# Revit family: 879-106X99-001-DN50-250
name_source: partatom
category: Pipe Accessories
units: mm (PartAtom-declared; Revit-internal decimal feet)

## family parameters
Always vertical = Yes
Cut with Voids When Loaded = No
Part Type = Valve - Breaks Into
Round Connector Dimension = Use Diameter
Shared = No
Work Plane-Based = No

## types (36) — shared parameters
879-0050-10-14400609999 = DN50_PN10/16
879-0050-10-14400619999 = DN50_PN10/16
879-0050-10-14400629999 = DN50_PN10/16
879-0050-10-144006299A0 = DN50_PN10/16
879-0065-10-14400609999 = DN65_PN10/16
879-0065-10-14400619999 = DN65_PN10/16
879-0065-10-14400629999 = DN65_PN10/16
879-0065-10-144006299A0 = DN65_PN10/16
879-0080-10-14400609999 = DN80_PN10/16
879-0080-10-14400619999 = DN80_PN10/16
879-0080-10-14400629999 = DN80_PN10/16
879-0080-10-144006299A0 = DN80_PN10/16
879-0100-10-14400609999 = DN100_PN10/16
879-0100-10-14400619999 = DN100_PN10/16
879-0100-10-14400629999 = DN100_PN10/16
879-0100-10-144006299A0 = DN100_PN10/16
879-0150-10-14400609999 = DN150_PN10/16
879-0150-10-14400619999 = DN150_PN10/16
879-0150-10-14400629999 = DN150_PN10/16
879-0150-10-144006299A0 = DN150_PN10/16
879-0200-10-04400609999 = DN200_PN10
879-0200-10-04400619999 = DN200_PN10
879-0200-10-04400629999 = DN200_PN10
879-0200-10-044006299A0 = DN200_PN10
879-0200-10-14400609999 = DN200_PN16
879-0200-10-14400619999 = DN200_PN16
879-0200-10-14400629999 = DN200_PN16
879-0200-10-144006299A0 = DN200_PN16
879-0250-10-04400609999 = DN250_PN10
879-0250-10-04400619999 = DN250_PN10
879-0250-10-04400629999 = DN250_PN10
879-0250-10-044006299A0 = DN250_PN10
879-0250-10-14400609999 = DN250_PN16
879-0250-10-14400619999 = DN250_PN16
879-0250-10-14400629999 = DN250_PN16
879-0250-10-144006299A0 = DN250_PN16
Body_wall_thickness = 10 mm  [stored 0.0328084 ft]
Description_ = AVK ON/OFF FLOAT LEVEL CONTROL VALVE
Search_Table = 879-106X99-001-DN50-250
URL product pages = https://www.avkvalves.com

## per-type parameters (varying)
- 879-0050-10-14400609999_DN50_PN10/16: Body_Collar_Dia=24 mm  [stored 0.0787402 ft]; Body_Collar_Dia_2=21 mm  [stored 0.0688976 ft]; Body_Flange_Dia=74 mm; Body_Flange_Dia_2=82 mm; Body_Height_1=58 mm; Body_Height_2=29 mm; Body_Height_3=45 mm; Body_Height_4=44 mm; Body_Top_Dia=10 mm  [stored 0.0328084 ft]; Body_Top_Dia_2=9 mm  [stored 0.0295276 ft]; Body_With_Dia=29 mm; Body_With_Dia_1=58 mm; Body_With_Dia_2=62 mm; Bolt_support=177 mm; Bolt_support_2=88 mm; Bolt_support_Dia=12 mm  [stored 0.0393701 ft]; Bolt_support_lenght=45 mm; Bolt_support_lenght_2=55 mm; Bottom_profile=13 mm; D1=50 mm; D3=83 mm; DN=50 mm; Fillet_Length=6 mm  [stored 0.019685 ft]; Fillet_Length_Ref=18 mm  [stored 0.0590551 ft]; Flange_thickness=19 mm  [stored 0.062336 ft]; H=290 mm; H3_Ref=284 mm; ID=25 mm  [stored 0.082021 ft]; L=230 mm; PG_Dia=25 mm  [stored 0.082021 ft]; PG_Ref=38 mm; PG_depth=8 mm  [stored 0.0262467 ft]; PG_height=180 mm; PG_height_1=167 mm; PG_ref=35 mm  [stored 0.114829 ft]; PR_1=14 mm  [stored 0.0459318 ft]; P_lenght=33 mm  [stored 0.108268 ft]; Pilot_Dia_1=15 mm  [stored 0.0492126 ft]; Pilot_Dia_2=30 mm  [stored 0.0984252 ft]; Pilot_Dia_3=10 mm  [stored 0.0328084 ft]; Pilot_Dia_4=5 mm  [stored 0.0164042 ft]; Pilot_Dia_5=3 mm  [stored 0.00984252 ft]; Pilot_top_1=174 mm; Pilot_top_ref=18 mm  [stored 0.0590551 ft]; Profile1_Height=100 mm; Profile1_Length=22 mm  [stored 0.0721785 ft]; Profile1_Length_2=15 mm  [stored 0.0492126 ft]; Profile_Dia=6 mm  [stored 0.019685 ft]; Profile_Dia_2=6 mm  [stored 0.019685 ft]; Profile_Dia_3=12 mm  [stored 0.0393701 ft]; Profile_height ref=41 mm; T_Height=61 mm; T_Height_2=52 mm; T_Height_Ref_1=9 mm  [stored 0.0295276 ft]; T_Height_Ref_2=10 mm  [stored 0.0328084 ft]; Top_Profile=106 mm; Top_Profile_Ref=111 mm; W=252 mm; W_Ref=246 mm
- 879-0050-10-14400619999_DN50_PN10/16: Body_Collar_Dia=24 mm  [stored 0.0787402 ft]; Body_Collar_Dia_2=21 mm  [stored 0.0688976 ft]; Body_Flange_Dia=74 mm; Body_Flange_Dia_2=82 mm; Body_Height_1=58 mm; Body_Height_2=29 mm; Body_Height_3=50 mm; Body_Height_4=44 mm; Body_Top_Dia=10 mm  [stored 0.0328084 ft]; Body_Top_Dia_2=9 mm  [stored 0.0295276 ft]; Body_With_Dia=29 mm; Body_With_Dia_1=58 mm; Body_With_Dia_2=62 mm; Bolt_support=177 mm; Bolt_support_2=88 mm; Bolt_support_Dia=12 mm  [stored 0.0393701 ft]; Bolt_support_lenght=45 mm; Bolt_support_lenght_2=55 mm; Bottom_profile=13 mm; D1=50 mm; D3=83 mm; DN=50 mm; Fillet_Length=6 mm  [stored 0.019685 ft]; Fillet_Length_Ref=18 mm  [stored 0.0590551 ft]; Flange_thickness=19 mm  [stored 0.062336 ft]; H=290 mm; H3_Ref=284 mm; ID=25 mm  [stored 0.082021 ft]; L=230 mm; PG_Dia=25 mm  [stored 0.082021 ft]; PG_Ref=38 mm; PG_depth=8 mm  [stored 0.0262467 ft]; PG_height=187 mm; PG_height_1=175 mm; PG_ref=35 mm  [stored 0.114829 ft]; PR_1=11 mm; P_lenght=33 mm  [stored 0.108268 ft]; Pilot_Dia_1=15 mm  [stored 0.0492126 ft]; Pilot_Dia_2=30 mm  [stored 0.0984252 ft]; Pilot_Dia_3=10 mm  [stored 0.0328084 ft]; Pilot_Dia_4=5 mm  [stored 0.0164042 ft]; Pilot_Dia_5=3 mm  [stored 0.00984252 ft]; Pilot_top_1=176 mm; Pilot_top_ref=15 mm  [stored 0.0492126 ft]; Profile1_Height=110 mm; Profile1_Length=22 mm  [stored 0.0721785 ft]; Profile1_Length_2=15 mm  [stored 0.0492126 ft]; Profile_Dia=6 mm  [stored 0.019685 ft]; Profile_Dia_2=6 mm  [stored 0.019685 ft]; Profile_Dia_3=12 mm  [stored 0.0393701 ft]; Profile_height ref=41 mm; T_Height=51 mm; T_Height_2=43 mm; T_Height_Ref_1=7 mm  [stored 0.0229659 ft]; T_Height_Ref_2=8 mm  [stored 0.0262467 ft]; Top_Profile=106 mm; Top_Profile_Ref=111 mm; W=252 mm; W_Ref=246 mm
- 879-0050-10-14400629999_DN50_PN10/16: Body_Collar_Dia=24 mm  [stored 0.0787402 ft]; Body_Collar_Dia_2=21 mm  [stored 0.0688976 ft]; Body_Flange_Dia=74 mm; Body_Flange_Dia_2=82 mm; Body_Height_1=58 mm; Body_Height_2=29 mm; Body_Height_3=45 mm; Body_Height_4=44 mm; Body_Top_Dia=10 mm  [stored 0.0328084 ft]; Body_Top_Dia_2=9 mm  [stored 0.0295276 ft]; Body_With_Dia=29 mm; Body_With_Dia_1=58 mm; Body_With_Dia_2=62 mm; Bolt_support=177 mm; Bolt_support_2=88 mm; Bolt_support_Dia=12 mm  [stored 0.0393701 ft]; Bolt_support_lenght=45 mm; Bolt_support_lenght_2=55 mm; Bottom_profile=13 mm; D1=50 mm; D3=83 mm; DN=50 mm; Fillet_Length=6 mm  [stored 0.019685 ft]; Fillet_Length_Ref=18 mm  [stored 0.0590551 ft]; Flange_thickness=19 mm  [stored 0.062336 ft]; H=290 mm; H3_Ref=284 mm; ID=25 mm  [stored 0.082021 ft]; L=230 mm; PG_Dia=25 mm  [stored 0.082021 ft]; PG_Ref=38 mm; PG_depth=8 mm  [stored 0.0262467 ft]; PG_height=180 mm; PG_height_1=167 mm; PG_ref=35 mm  [stored 0.114829 ft]; PR_1=14 mm  [stored 0.0459318 ft]; P_lenght=33 mm  [stored 0.108268 ft]; Pilot_Dia_1=15 mm  [stored 0.0492126 ft]; Pilot_Dia_2=30 mm  [stored 0.0984252 ft]; Pilot_Dia_3=10 mm  [stored 0.0328084 ft]; Pilot_Dia_4=5 mm  [stored 0.0164042 ft]; Pilot_Dia_5=3 mm  [stored 0.00984252 ft]; Pilot_top_1=174 mm; Pilot_top_ref=18 mm  [stored 0.0590551 ft]; Profile1_Height=100 mm; Profile1_Length=22 mm  [stored 0.0721785 ft]; Profile1_Length_2=15 mm  [stored 0.0492126 ft]; Profile_Dia=6 mm  [stored 0.019685 ft]; Profile_Dia_2=6 mm  [stored 0.019685 ft]; Profile_Dia_3=12 mm  [stored 0.0393701 ft]; Profile_height ref=41 mm; T_Height=61 mm; T_Height_2=52 mm; T_Height_Ref_1=9 mm  [stored 0.0295276 ft]; T_Height_Ref_2=10 mm  [stored 0.0328084 ft]; Top_Profile=106 mm; Top_Profile_Ref=111 mm; W=252 mm; W_Ref=246 mm
- 879-0050-10-144006299A0_DN50_PN10/16: Body_Collar_Dia=24 mm  [stored 0.0787402 ft]; Body_Collar_Dia_2=21 mm  [stored 0.0688976 ft]; Body_Flange_Dia=74 mm; Body_Flange_Dia_2=82 mm; Body_Height_1=58 mm; Body_Height_2=29 mm; Body_Height_3=50 mm; Body_Height_4=44 mm; Body_Top_Dia=10 mm  [stored 0.0328084 ft]; Body_Top_Dia_2=9 mm  [stored 0.0295276 ft]; Body_With_Dia=29 mm; Body_With_Dia_1=58 mm; Body_With_Dia_2=62 mm; Bolt_support=177 mm; Bolt_support_2=88 mm; Bolt_support_Dia=12 mm  [stored 0.0393701 ft]; Bolt_support_lenght=45 mm; Bolt_support_lenght_2=55 mm; Bottom_profile=13 mm; D1=50 mm; D3=83 mm; DN=50 mm; Fillet_Length=6 mm  [stored 0.019685 ft]; Fillet_Length_Ref=18 mm  [stored 0.0590551 ft]; Flange_thickness=19 mm  [stored 0.062336 ft]; H=407 mm; H3_Ref=401 mm; ID=25 mm  [stored 0.082021 ft]; L=230 mm; PG_Dia=25 mm  [stored 0.082021 ft]; PG_Ref=38 mm; PG_depth=8 mm  [stored 0.0262467 ft]; PG_height=214 mm; PG_height_1=201 mm; PG_ref=35 mm  [stored 0.114829 ft]; PR_1=38 mm; P_lenght=33 mm  [stored 0.108268 ft]; Pilot_Dia_1=15 mm  [stored 0.0492126 ft]; Pilot_Dia_2=30 mm  [stored 0.0984252 ft]; Pilot_Dia_3=10 mm  [stored 0.0328084 ft]; Pilot_Dia_4=5 mm  [stored 0.0164042 ft]; Pilot_Dia_5=3 mm  [stored 0.00984252 ft]; Pilot_top_1=235 mm; Pilot_top_ref=74 mm; Profile1_Height=110 mm; Profile1_Length=22 mm  [stored 0.0721785 ft]; Profile1_Length_2=15 mm  [stored 0.0492126 ft]; Profile_Dia=6 mm  [stored 0.019685 ft]; Profile_Dia_2=6 mm  [stored 0.019685 ft]; Profile_Dia_3=12 mm  [stored 0.0393701 ft]; Profile_height ref=41 mm; T_Height=168 mm; T_Height_2=144 mm; T_Height_Ref_1=24 mm  [stored 0.0787402 ft]; T_Height_Ref_2=28 mm; Top_Profile=106 mm; Top_Profile_Ref=111 mm; W=252 mm; W_Ref=246 mm
- 879-0065-10-14400609999_DN65_PN10/16: Body_Collar_Dia=30 mm  [stored 0.0984252 ft]; Body_Collar_Dia_2=26 mm; Body_Flange_Dia=94 mm; Body_Flange_Dia_2=104 mm; Body_Height_1=73 mm; Body_Height_2=36 mm; Body_Height_3=58 mm; Body_Height_4=51 mm; Body_Top_Dia=13 mm; Body_Top_Dia_2=11 mm; Body_With_Dia=36 mm; Body_With_Dia_1=73 mm; Body_With_Dia_2=78 mm; Bolt_support=223 mm; Bolt_support_2=112 mm; Bolt_support_Dia=12 mm  [stored 0.0393701 ft]; Bolt_support_lenght=53 mm; Bolt_support_lenght_2=63 mm; Bottom_profile=16 mm  [stored 0.0524934 ft]; D1=59 mm; D3=93 mm; DN=65 mm; Fillet_Length=6 mm  [stored 0.019685 ft]; Fillet_Length_Ref=18 mm  [stored 0.0590551 ft]; Flange_thickness=19 mm  [stored 0.062336 ft]; H=305 mm; H3_Ref=299 mm; ID=33 mm  [stored 0.108268 ft]; L=290 mm; PG_Dia=33 mm  [stored 0.108268 ft]; PG_Ref=48 mm; PG_depth=8 mm  [stored 0.0262467 ft]; PG_height=201 mm; PG_height_1=185 mm; PG_ref=43 mm; PR_1=11 mm; P_lenght=39 mm  [stored 0.127953 ft]; Pilot_Dia_1=18 mm  [stored 0.0590551 ft]; Pilot_Dia_2=35 mm  [stored 0.114829 ft]; Pilot_Dia_3=12 mm  [stored 0.0393701 ft]; Pilot_Dia_4=6 mm  [stored 0.019685 ft]; Pilot_Dia_5=4 mm  [stored 0.0131234 ft]; Pilot_top_1=194 mm; Pilot_top_ref=2 mm  [stored 0.00656168 ft]; Profile1_Height=117 mm; Profile1_Length=25 mm  [stored 0.082021 ft]; Profile1_Length_2=17 mm; Profile_Dia=6 mm  [stored 0.019685 ft]; Profile_Dia_2=6 mm  [stored 0.019685 ft]; Profile_Dia_3=12 mm  [stored 0.0393701 ft]; Profile_height ref=41 mm; T_Height=49 mm; T_Height_2=42 mm; T_Height_Ref_1=7 mm  [stored 0.0229659 ft]; T_Height_Ref_2=8 mm  [stored 0.0262467 ft]; Top_Profile=134 mm; Top_Profile_Ref=139 mm; W=275 mm; W_Ref=269 mm
- 879-0065-10-14400619999_DN65_PN10/16: Body_Collar_Dia=30 mm  [stored 0.0984252 ft]; Body_Collar_Dia_2=26 mm; Body_Flange_Dia=94 mm; Body_Flange_Dia_2=104 mm; Body_Height_1=73 mm; Body_Height_2=36 mm; Body_Height_3=58 mm; Body_Height_4=51 mm; Body_Top_Dia=13 mm; Body_Top_Dia_2=11 mm; Body_With_Dia=36 mm; Body_With_Dia_1=73 mm; Body_With_Dia_2=78 mm; Bolt_support=223 mm; Bolt_support_2=112 mm; Bolt_support_Dia=12 mm  [stored 0.0393701 ft]; Bolt_support_lenght=53 mm; Bolt_support_lenght_2=63 mm; Bottom_profile=16 mm  [stored 0.0524934 ft]; D1=59 mm; D3=93 mm; DN=65 mm; Fillet_Length=6 mm  [stored 0.019685 ft]; Fillet_Length_Ref=18 mm  [stored 0.0590551 ft]; Flange_thickness=19 mm  [stored 0.062336 ft]; H=305 mm; H3_Ref=299 mm; ID=33 mm  [stored 0.108268 ft]; L=290 mm; PG_Dia=33 mm  [stored 0.108268 ft]; PG_Ref=48 mm; PG_depth=8 mm  [stored 0.0262467 ft]; PG_height=215 mm; PG_height_1=199 mm; PG_ref=43 mm; PR_1=7 mm  [stored 0.0229659 ft]; P_lenght=39 mm  [stored 0.127953 ft]; Pilot_Dia_1=18 mm  [stored 0.0590551 ft]; Pilot_Dia_2=35 mm  [stored 0.114829 ft]; Pilot_Dia_3=12 mm  [stored 0.0393701 ft]; Pilot_Dia_4=6 mm  [stored 0.019685 ft]; Pilot_Dia_5=4 mm  [stored 0.0131234 ft]; Pilot_top_1=194 mm; Pilot_top_ref=2 mm  [stored 0.00656168 ft]; Profile1_Height=135 mm; Profile1_Length=25 mm  [stored 0.082021 ft]; Profile1_Length_2=17 mm; Profile_Dia=6 mm  [stored 0.019685 ft]; Profile_Dia_2=6 mm  [stored 0.019685 ft]; Profile_Dia_3=12 mm  [stored 0.0393701 ft]; Profile_height ref=41 mm; T_Height=31 mm  [stored 0.101706 ft]; T_Height_2=26 mm; T_Height_Ref_1=4 mm  [stored 0.0131234 ft]; T_Height_Ref_2=5 mm  [stored 0.0164042 ft]; Top_Profile=134 mm; Top_Profile_Ref=139 mm; W=275 mm; W_Ref=269 mm
- 879-0065-10-14400629999_DN65_PN10/16: Body_Collar_Dia=30 mm  [stored 0.0984252 ft]; Body_Collar_Dia_2=26 mm; Body_Flange_Dia=94 mm; Body_Flange_Dia_2=104 mm; Body_Height_1=73 mm; Body_Height_2=36 mm; Body_Height_3=58 mm; Body_Height_4=51 mm; Body_Top_Dia=13 mm; Body_Top_Dia_2=11 mm; Body_With_Dia=36 mm; Body_With_Dia_1=73 mm; Body_With_Dia_2=78 mm; Bolt_support=223 mm; Bolt_support_2=112 mm; Bolt_support_Dia=12 mm  [stored 0.0393701 ft]; Bolt_support_lenght=53 mm; Bolt_support_lenght_2=63 mm; Bottom_profile=16 mm  [stored 0.0524934 ft]; D1=59 mm; D3=93 mm; DN=65 mm; Fillet_Length=6 mm  [stored 0.019685 ft]; Fillet_Length_Ref=18 mm  [stored 0.0590551 ft]; Flange_thickness=19 mm  [stored 0.062336 ft]; H=305 mm; H3_Ref=299 mm; ID=33 mm  [stored 0.108268 ft]; L=290 mm; PG_Dia=33 mm  [stored 0.108268 ft]; PG_Ref=48 mm; PG_depth=8 mm  [stored 0.0262467 ft]; PG_height=202 mm; PG_height_1=185 mm; PG_ref=43 mm; PR_1=11 mm; P_lenght=39 mm  [stored 0.127953 ft]; Pilot_Dia_1=18 mm  [stored 0.0590551 ft]; Pilot_Dia_2=35 mm  [stored 0.114829 ft]; Pilot_Dia_3=12 mm  [stored 0.0393701 ft]; Pilot_Dia_4=6 mm  [stored 0.019685 ft]; Pilot_Dia_5=4 mm  [stored 0.0131234 ft]; Pilot_top_1=194 mm; Pilot_top_ref=2 mm  [stored 0.00656168 ft]; Profile1_Height=117 mm; Profile1_Length=25 mm  [stored 0.082021 ft]; Profile1_Length_2=17 mm; Profile_Dia=6 mm  [stored 0.019685 ft]; Profile_Dia_2=6 mm  [stored 0.019685 ft]; Profile_Dia_3=12 mm  [stored 0.0393701 ft]; Profile_height ref=41 mm; T_Height=49 mm; T_Height_2=42 mm; T_Height_Ref_1=7 mm  [stored 0.0229659 ft]; T_Height_Ref_2=8 mm  [stored 0.0262467 ft]; Top_Profile=134 mm; Top_Profile_Ref=139 mm; W=275 mm; W_Ref=269 mm
- 879-0065-10-144006299A0_DN65_PN10/16: Body_Collar_Dia=30 mm  [stored 0.0984252 ft]; Body_Collar_Dia_2=26 mm; Body_Flange_Dia=94 mm; Body_Flange_Dia_2=104 mm; Body_Height_1=73 mm; Body_Height_2=36 mm; Body_Height_3=73 mm; Body_Height_4=51 mm; Body_Top_Dia=13 mm; Body_Top_Dia_2=11 mm; Body_With_Dia=36 mm; Body_With_Dia_1=73 mm; Body_With_Dia_2=78 mm; Bolt_support=223 mm; Bolt_support_2=112 mm; Bolt_support_Dia=12 mm  [stored 0.0393701 ft]; Bolt_support_lenght=53 mm; Bolt_support_lenght_2=63 mm; Bottom_profile=16 mm  [stored 0.0524934 ft]; D1=59 mm; D3=93 mm; DN=65 mm; Fillet_Length=6 mm  [stored 0.019685 ft]; Fillet_Length_Ref=18 mm  [stored 0.0590551 ft]; Flange_thickness=19 mm  [stored 0.062336 ft]; H=436 mm; H3_Ref=430 mm; ID=33 mm  [stored 0.108268 ft]; L=290 mm; PG_Dia=33 mm  [stored 0.108268 ft]; PG_Ref=48 mm; PG_depth=8 mm  [stored 0.0262467 ft]; PG_height=245 mm; PG_height_1=229 mm; PG_ref=43 mm; PR_1=37 mm; P_lenght=39 mm  [stored 0.127953 ft]; Pilot_Dia_1=18 mm  [stored 0.0590551 ft]; Pilot_Dia_2=35 mm  [stored 0.114829 ft]; Pilot_Dia_3=12 mm  [stored 0.0393701 ft]; Pilot_Dia_4=6 mm  [stored 0.019685 ft]; Pilot_Dia_5=4 mm  [stored 0.0131234 ft]; Pilot_top_1=267 mm; Pilot_top_ref=61 mm; Profile1_Height=135 mm; Profile1_Length=25 mm  [stored 0.082021 ft]; Profile1_Length_2=17 mm; Profile_Dia=6 mm  [stored 0.019685 ft]; Profile_Dia_2=6 mm  [stored 0.019685 ft]; Profile_Dia_3=12 mm  [stored 0.0393701 ft]; Profile_height ref=41 mm; T_Height=162 mm; T_Height_2=138 mm; T_Height_Ref_1=23 mm  [stored 0.0754593 ft]; T_Height_Ref_2=27 mm; Top_Profile=134 mm; Top_Profile_Ref=139 mm; W=275 mm; W_Ref=269 mm
- 879-0080-10-14400609999_DN80_PN10/16: Body_Collar_Dia=32 mm; Body_Collar_Dia_2=28 mm; Body_Flange_Dia=100 mm; Body_Flange_Dia_2=111 mm; Body_Height_1=78 mm; Body_Height_2=39 mm  [stored 0.127953 ft]; Body_Height_3=62 mm; Body_Height_4=54 mm; Body_Top_Dia=14 mm  [stored 0.0459318 ft]; Body_Top_Dia_2=12 mm  [stored 0.0393701 ft]; Body_With_Dia=39 mm  [stored 0.127953 ft]; Body_With_Dia_1=78 mm; Body_With_Dia_2=84 mm; Bolt_support=238 mm; Bolt_support_2=119 mm; Bolt_support_Dia=12 mm  [stored 0.0393701 ft]; Bolt_support_lenght=60 mm; Bolt_support_lenght_2=70 mm; Bottom_profile=20 mm  [stored 0.0656168 ft]; D1=66 mm; D3=100 mm; DN=80 mm; Fillet_Length=6 mm  [stored 0.019685 ft]; Fillet_Length_Ref=18 mm  [stored 0.0590551 ft]; Flange_thickness=19 mm  [stored 0.062336 ft]; H=320 mm; H3_Ref=314 mm; ID=40 mm  [stored 0.131234 ft]; L=310 mm; PG_Dia=40 mm  [stored 0.131234 ft]; PG_Ref=52 mm; PG_depth=8 mm  [stored 0.0262467 ft]; PG_height=232 mm; PG_height_1=212 mm; PG_ref=50 mm; PR_1=7 mm  [stored 0.0229659 ft]; P_lenght=43 mm; Pilot_Dia_1=20 mm  [stored 0.0656168 ft]; Pilot_Dia_2=39 mm  [stored 0.127953 ft]; Pilot_Dia_3=13 mm; Pilot_Dia_4=7 mm  [stored 0.0229659 ft]; Pilot_Dia_5=4 mm  [stored 0.0131234 ft]; Pilot_top_1=204 mm; Pilot_top_ref=0 mm  [stored 0 ft]; Profile1_Height=144 mm; Profile1_Length=27 mm; Profile1_Length_2=18 mm  [stored 0.0590551 ft]; Profile_Dia=6 mm  [stored 0.019685 ft]; Profile_Dia_2=6 mm  [stored 0.019685 ft]; Profile_Dia_3=12 mm  [stored 0.0393701 ft]; Profile_height ref=41 mm; T_Height=29 mm; T_Height_2=25 mm  [stored 0.082021 ft]; T_Height_Ref_1=4 mm  [stored 0.0131234 ft]; T_Height_Ref_2=5 mm  [stored 0.0164042 ft]; Top_Profile=143 mm; Top_Profile_Ref=148 mm; W=290 mm; W_Ref=284 mm
- 879-0080-10-14400619999_DN80_PN10/16: Body_Collar_Dia=32 mm; Body_Collar_Dia_2=28 mm; Body_Flange_Dia=100 mm; Body_Flange_Dia_2=111 mm; Body_Height_1=78 mm; Body_Height_2=39 mm  [stored 0.127953 ft]; Body_Height_3=62 mm; Body_Height_4=54 mm; Body_Top_Dia=14 mm  [stored 0.0459318 ft]; Body_Top_Dia_2=12 mm  [stored 0.0393701 ft]; Body_With_Dia=39 mm  [stored 0.127953 ft]; Body_With_Dia_1=78 mm; Body_With_Dia_2=84 mm; Bolt_support=238 mm; Bolt_support_2=119 mm; Bolt_support_Dia=12 mm  [stored 0.0393701 ft]; Bolt_support_lenght=60 mm; Bolt_support_lenght_2=70 mm; Bottom_profile=20 mm  [stored 0.0656168 ft]; D1=66 mm; D3=100 mm; DN=80 mm; Fillet_Length=6 mm  [stored 0.019685 ft]; Fillet_Length_Ref=18 mm  [stored 0.0590551 ft]; Flange_thickness=19 mm  [stored 0.062336 ft]; H=320 mm; H3_Ref=314 mm; ID=40 mm  [stored 0.131234 ft]; L=310 mm; PG_Dia=40 mm  [stored 0.131234 ft]; PG_Ref=52 mm; PG_depth=8 mm  [stored 0.0262467 ft]; PG_height=223 mm; PG_height_1=203 mm; PG_ref=50 mm; PR_1=9 mm  [stored 0.0295276 ft]; P_lenght=43 mm; Pilot_Dia_1=20 mm  [stored 0.0656168 ft]; Pilot_Dia_2=39 mm  [stored 0.127953 ft]; Pilot_Dia_3=13 mm; Pilot_Dia_4=7 mm  [stored 0.0229659 ft]; Pilot_Dia_5=4 mm  [stored 0.0131234 ft]; Pilot_top_1=204 mm; Pilot_top_ref=0 mm  [stored 0 ft]; Profile1_Height=133 mm; Profile1_Length=27 mm; Profile1_Length_2=18 mm  [stored 0.0590551 ft]; Profile_Dia=6 mm  [stored 0.019685 ft]; Profile_Dia_2=6 mm  [stored 0.019685 ft]; Profile_Dia_3=12 mm  [stored 0.0393701 ft]; Profile_height ref=41 mm; T_Height=40 mm  [stored 0.131234 ft]; T_Height_2=34 mm; T_Height_Ref_1=6 mm  [stored 0.019685 ft]; T_Height_Ref_2=7 mm  [stored 0.0229659 ft]; Top_Profile=143 mm; Top_Profile_Ref=148 mm; W=290 mm; W_Ref=284 mm
- 879-0080-10-14400629999_DN80_PN10/16: Body_Collar_Dia=32 mm; Body_Collar_Dia_2=28 mm; Body_Flange_Dia=100 mm; Body_Flange_Dia_2=111 mm; Body_Height_1=78 mm; Body_Height_2=39 mm  [stored 0.127953 ft]; Body_Height_3=62 mm; Body_Height_4=54 mm; Body_Top_Dia=14 mm  [stored 0.0459318 ft]; Body_Top_Dia_2=12 mm  [stored 0.0393701 ft]; Body_With_Dia=39 mm  [stored 0.127953 ft]; Body_With_Dia_1=78 mm; Body_With_Dia_2=84 mm; Bolt_support=238 mm; Bolt_support_2=119 mm; Bolt_support_Dia=12 mm  [stored 0.0393701 ft]; Bolt_support_lenght=60 mm; Bolt_support_lenght_2=70 mm; Bottom_profile=20 mm  [stored 0.0656168 ft]; D1=66 mm; D3=100 mm; DN=80 mm; Fillet_Length=6 mm  [stored 0.019685 ft]; Fillet_Length_Ref=18 mm  [stored 0.0590551 ft]; Flange_thickness=19 mm  [stored 0.062336 ft]; H=320 mm; H3_Ref=314 mm; ID=40 mm  [stored 0.131234 ft]; L=310 mm; PG_Dia=40 mm  [stored 0.131234 ft]; PG_Ref=52 mm; PG_depth=8 mm  [stored 0.0262467 ft]; PG_height=232 mm; PG_height_1=212 mm; PG_ref=50 mm; PR_1=7 mm  [stored 0.0229659 ft]; P_lenght=43 mm; Pilot_Dia_1=20 mm  [stored 0.0656168 ft]; Pilot_Dia_2=39 mm  [stored 0.127953 ft]; Pilot_Dia_3=13 mm; Pilot_Dia_4=7 mm  [stored 0.0229659 ft]; Pilot_Dia_5=4 mm  [stored 0.0131234 ft]; Pilot_top_1=204 mm; Pilot_top_ref=0 mm  [stored 0 ft]; Profile1_Height=144 mm; Profile1_Length=27 mm; Profile1_Length_2=18 mm  [stored 0.0590551 ft]; Profile_Dia=6 mm  [stored 0.019685 ft]; Profile_Dia_2=6 mm  [stored 0.019685 ft]; Profile_Dia_3=12 mm  [stored 0.0393701 ft]; Profile_height ref=41 mm; T_Height=29 mm; T_Height_2=25 mm  [stored 0.082021 ft]; T_Height_Ref_1=4 mm  [stored 0.0131234 ft]; T_Height_Ref_2=5 mm  [stored 0.0164042 ft]; Top_Profile=143 mm; Top_Profile_Ref=148 mm; W=290 mm; W_Ref=284 mm
- 879-0080-10-144006299A0_DN80_PN10/16: Body_Collar_Dia=32 mm; Body_Collar_Dia_2=28 mm; Body_Flange_Dia=100 mm; Body_Flange_Dia_2=111 mm; Body_Height_1=78 mm; Body_Height_2=39 mm  [stored 0.127953 ft]; Body_Height_3=78 mm; Body_Height_4=54 mm; Body_Top_Dia=14 mm  [stored 0.0459318 ft]; Body_Top_Dia_2=12 mm  [stored 0.0393701 ft]; Body_With_Dia=39 mm  [stored 0.127953 ft]; Body_With_Dia_1=78 mm; Body_With_Dia_2=84 mm; Bolt_support=238 mm; Bolt_support_2=119 mm; Bolt_support_Dia=12 mm  [stored 0.0393701 ft]; Bolt_support_lenght=60 mm; Bolt_support_lenght_2=70 mm; Bottom_profile=20 mm  [stored 0.0656168 ft]; D1=66 mm; D3=100 mm; DN=80 mm; Fillet_Length=6 mm  [stored 0.019685 ft]; Fillet_Length_Ref=18 mm  [stored 0.0590551 ft]; Flange_thickness=19 mm  [stored 0.062336 ft]; H=451 mm; H3_Ref=445 mm; ID=40 mm  [stored 0.131234 ft]; L=310 mm; PG_Dia=40 mm  [stored 0.131234 ft]; PG_Ref=52 mm; PG_depth=8 mm  [stored 0.0262467 ft]; PG_height=253 mm; PG_height_1=233 mm; PG_ref=50 mm; PR_1=39 mm  [stored 0.127953 ft]; P_lenght=43 mm; Pilot_Dia_1=20 mm  [stored 0.0656168 ft]; Pilot_Dia_2=39 mm  [stored 0.127953 ft]; Pilot_Dia_3=13 mm; Pilot_Dia_4=7 mm  [stored 0.0229659 ft]; Pilot_Dia_5=4 mm  [stored 0.0131234 ft]; Pilot_top_1=277 mm; Pilot_top_ref=58 mm; Profile1_Height=133 mm; Profile1_Length=27 mm; Profile1_Length_2=18 mm  [stored 0.0590551 ft]; Profile_Dia=6 mm  [stored 0.019685 ft]; Profile_Dia_2=6 mm  [stored 0.019685 ft]; Profile_Dia_3=12 mm  [stored 0.0393701 ft]; Profile_height ref=41 mm; T_Height=171 mm; T_Height_2=147 mm; T_Height_Ref_1=24 mm  [stored 0.0787402 ft]; T_Height_Ref_2=29 mm; Top_Profile=143 mm; Top_Profile_Ref=148 mm; W=290 mm; W_Ref=284 mm
- 879-0100-10-14400609999_DN100_PN10/16: Body_Collar_Dia=36 mm; Body_Collar_Dia_2=31 mm  [stored 0.101706 ft]; Body_Flange_Dia=113 mm; Body_Flange_Dia_2=125 mm; Body_Height_1=88 mm; Body_Height_2=44 mm; Body_Height_3=59 mm; Body_Height_4=59 mm; Body_Top_Dia=16 mm  [stored 0.0524934 ft]; Body_Top_Dia_2=13 mm; Body_With_Dia=44 mm; Body_With_Dia_1=88 mm; Body_With_Dia_2=95 mm; Bolt_support=269 mm; Bolt_support_2=135 mm; Bolt_support_Dia=12 mm  [stored 0.0393701 ft]; Bolt_support_lenght=70 mm; Bolt_support_lenght_2=80 mm; Bottom_profile=25 mm  [stored 0.082021 ft]; D1=78 mm; D3=110 mm; DN=100 mm; Fillet_Length=6 mm  [stored 0.019685 ft]; Fillet_Length_Ref=18 mm  [stored 0.0590551 ft]; Flange_thickness=19 mm  [stored 0.062336 ft]; H=340 mm; H3_Ref=334 mm; ID=50 mm; L=350 mm; PG_Dia=50 mm; PG_Ref=58 mm; PG_depth=8 mm  [stored 0.0262467 ft]; PG_height=248 mm; PG_height_1=223 mm; PG_ref=60 mm; PR_1=7 mm  [stored 0.0229659 ft]; P_lenght=48 mm; Pilot_Dia_1=22 mm  [stored 0.0721785 ft]; Pilot_Dia_2=44 mm; Pilot_Dia_3=15 mm  [stored 0.0492126 ft]; Pilot_Dia_4=7 mm  [stored 0.0229659 ft]; Pilot_Dia_5=5 mm  [stored 0.0164042 ft]; Pilot_top_1=214 mm; Pilot_top_ref=0 mm  [stored 0 ft]; Profile1_Height=150 mm; Profile1_Length=30 mm  [stored 0.0984252 ft]; Profile1_Length_2=20 mm  [stored 0.0656168 ft]; Profile_Dia=6 mm  [stored 0.019685 ft]; Profile_Dia_2=6 mm  [stored 0.019685 ft]; Profile_Dia_3=12 mm  [stored 0.0393701 ft]; Profile_height ref=41 mm; T_Height=33 mm  [stored 0.108268 ft]; T_Height_2=28 mm; T_Height_Ref_1=5 mm  [stored 0.0164042 ft]; T_Height_Ref_2=6 mm  [stored 0.019685 ft]; Top_Profile=162 mm; Top_Profile_Ref=167 mm; W=310 mm; W_Ref=304 mm
- 879-0100-10-14400619999_DN100_PN10/16: Body_Collar_Dia=36 mm; Body_Collar_Dia_2=31 mm  [stored 0.101706 ft]; Body_Flange_Dia=113 mm; Body_Flange_Dia_2=125 mm; Body_Height_1=88 mm; Body_Height_2=44 mm; Body_Height_3=59 mm; Body_Height_4=59 mm; Body_Top_Dia=16 mm  [stored 0.0524934 ft]; Body_Top_Dia_2=13 mm; Body_With_Dia=44 mm; Body_With_Dia_1=88 mm; Body_With_Dia_2=95 mm; Bolt_support=269 mm; Bolt_support_2=135 mm; Bolt_support_Dia=12 mm  [stored 0.0393701 ft]; Bolt_support_lenght=70 mm; Bolt_support_lenght_2=80 mm; Bottom_profile=25 mm  [stored 0.082021 ft]; D1=78 mm; D3=110 mm; DN=100 mm; Fillet_Length=6 mm  [stored 0.019685 ft]; Fillet_Length_Ref=18 mm  [stored 0.0590551 ft]; Flange_thickness=19 mm  [stored 0.062336 ft]; H=340 mm; H3_Ref=334 mm; ID=50 mm; L=350 mm; PG_Dia=50 mm; PG_Ref=58 mm; PG_depth=8 mm  [stored 0.0262467 ft]; PG_height=242 mm; PG_height_1=217 mm; PG_ref=60 mm; PR_1=10 mm  [stored 0.0328084 ft]; P_lenght=48 mm; Pilot_Dia_1=22 mm  [stored 0.0721785 ft]; Pilot_Dia_2=44 mm; Pilot_Dia_3=15 mm  [stored 0.0492126 ft]; Pilot_Dia_4=7 mm  [stored 0.0229659 ft]; Pilot_Dia_5=5 mm  [stored 0.0164042 ft]; Pilot_top_1=214 mm; Pilot_top_ref=0 mm  [stored 0 ft]; Profile1_Height=141 mm; Profile1_Length=30 mm  [stored 0.0984252 ft]; Profile1_Length_2=20 mm  [stored 0.0656168 ft]; Profile_Dia=6 mm  [stored 0.019685 ft]; Profile_Dia_2=6 mm  [stored 0.019685 ft]; Profile_Dia_3=12 mm  [stored 0.0393701 ft]; Profile_height ref=41 mm; T_Height=42 mm; T_Height_2=36 mm; T_Height_Ref_1=6 mm  [stored 0.019685 ft]; T_Height_Ref_2=7 mm  [stored 0.0229659 ft]; Top_Profile=162 mm; Top_Profile_Ref=167 mm; W=310 mm; W_Ref=304 mm
- 879-0100-10-14400629999_DN100_PN10/16: Body_Collar_Dia=36 mm; Body_Collar_Dia_2=31 mm  [stored 0.101706 ft]; Body_Flange_Dia=113 mm; Body_Flange_Dia_2=125 mm; Body_Height_1=88 mm; Body_Height_2=44 mm; Body_Height_3=59 mm; Body_Height_4=59 mm; Body_Top_Dia=16 mm  [stored 0.0524934 ft]; Body_Top_Dia_2=13 mm; Body_With_Dia=44 mm; Body_With_Dia_1=88 mm; Body_With_Dia_2=95 mm; Bolt_support=269 mm; Bolt_support_2=135 mm; Bolt_support_Dia=12 mm  [stored 0.0393701 ft]; Bolt_support_lenght=70 mm; Bolt_support_lenght_2=80 mm; Bottom_profile=25 mm  [stored 0.082021 ft]; D1=78 mm; D3=110 mm; DN=100 mm; Fillet_Length=6 mm  [stored 0.019685 ft]; Fillet_Length_Ref=18 mm  [stored 0.0590551 ft]; Flange_thickness=19 mm  [stored 0.062336 ft]; H=340 mm; H3_Ref=334 mm; ID=50 mm; L=350 mm; PG_Dia=50 mm; PG_Ref=58 mm; PG_depth=8 mm  [stored 0.0262467 ft]; PG_height=249 mm; PG_height_1=224 mm; PG_ref=60 mm; PR_1=7 mm  [stored 0.0229659 ft]; P_lenght=48 mm; Pilot_Dia_1=22 mm  [stored 0.0721785 ft]; Pilot_Dia_2=44 mm; Pilot_Dia_3=15 mm  [stored 0.0492126 ft]; Pilot_Dia_4=7 mm  [stored 0.0229659 ft]; Pilot_Dia_5=5 mm  [stored 0.0164042 ft]; Pilot_top_1=214 mm; Pilot_top_ref=0 mm  [stored 0 ft]; Profile1_Height=150 mm; Profile1_Length=30 mm  [stored 0.0984252 ft]; Profile1_Length_2=20 mm  [stored 0.0656168 ft]; Profile_Dia=6 mm  [stored 0.019685 ft]; Profile_Dia_2=6 mm  [stored 0.019685 ft]; Profile_Dia_3=12 mm  [stored 0.0393701 ft]; Profile_height ref=41 mm; T_Height=33 mm  [stored 0.108268 ft]; T_Height_2=28 mm; T_Height_Ref_1=5 mm  [stored 0.0164042 ft]; T_Height_Ref_2=6 mm  [stored 0.019685 ft]; Top_Profile=162 mm; Top_Profile_Ref=167 mm; W=310 mm; W_Ref=304 mm
- 879-0100-10-144006299A0_DN100_PN10/16: Body_Collar_Dia=36 mm; Body_Collar_Dia_2=31 mm  [stored 0.101706 ft]; Body_Flange_Dia=113 mm; Body_Flange_Dia_2=125 mm; Body_Height_1=88 mm; Body_Height_2=44 mm; Body_Height_3=70 mm; Body_Height_4=59 mm; Body_Top_Dia=16 mm  [stored 0.0524934 ft]; Body_Top_Dia_2=13 mm; Body_With_Dia=44 mm; Body_With_Dia_1=88 mm; Body_With_Dia_2=95 mm; Bolt_support=269 mm; Bolt_support_2=135 mm; Bolt_support_Dia=12 mm  [stored 0.0393701 ft]; Bolt_support_lenght=70 mm; Bolt_support_lenght_2=80 mm; Bottom_profile=25 mm  [stored 0.082021 ft]; D1=78 mm; D3=110 mm; DN=100 mm; Fillet_Length=6 mm  [stored 0.019685 ft]; Fillet_Length_Ref=18 mm  [stored 0.0590551 ft]; Flange_thickness=19 mm  [stored 0.062336 ft]; H=474 mm; H3_Ref=468 mm; ID=50 mm; L=350 mm; PG_Dia=50 mm; PG_Ref=58 mm; PG_depth=8 mm  [stored 0.0262467 ft]; PG_height=272 mm; PG_height_1=247 mm; PG_ref=60 mm; PR_1=40 mm  [stored 0.131234 ft]; P_lenght=48 mm; Pilot_Dia_1=22 mm  [stored 0.0721785 ft]; Pilot_Dia_2=44 mm; Pilot_Dia_3=15 mm  [stored 0.0492126 ft]; Pilot_Dia_4=7 mm  [stored 0.0229659 ft]; Pilot_Dia_5=5 mm  [stored 0.0164042 ft]; Pilot_top_1=287 mm; Pilot_top_ref=61 mm; Profile1_Height=141 mm; Profile1_Length=30 mm  [stored 0.0984252 ft]; Profile1_Length_2=20 mm  [stored 0.0656168 ft]; Profile_Dia=6 mm  [stored 0.019685 ft]; Profile_Dia_2=6 mm  [stored 0.019685 ft]; Profile_Dia_3=12 mm  [stored 0.0393701 ft]; Profile_height ref=41 mm; T_Height=176 mm; T_Height_2=151 mm; T_Height_Ref_1=25 mm  [stored 0.082021 ft]; T_Height_Ref_2=29 mm; Top_Profile=162 mm; Top_Profile_Ref=167 mm; W=310 mm; W_Ref=304 mm
- 879-0150-10-14400609999_DN150_PN10/16: Body_Collar_Dia=50 mm; Body_Collar_Dia_2=43 mm; Body_Flange_Dia=155 mm; Body_Flange_Dia_2=171 mm; Body_Height_1=120 mm; Body_Height_2=60 mm; Body_Height_3=60 mm; Body_Height_4=75 mm; Body_Top_Dia=22 mm  [stored 0.0721785 ft]; Body_Top_Dia_2=18 mm  [stored 0.0590551 ft]; Body_With_Dia=60 mm; Body_With_Dia_1=120 mm; Body_With_Dia_2=130 mm; Bolt_support=369 mm; Bolt_support_2=185 mm; Bolt_support_Dia=16 mm  [stored 0.0524934 ft]; Bolt_support_lenght=95 mm; Bolt_support_lenght_2=105 mm; Bottom_profile=38 mm; D1=106 mm; D3=143 mm; DN=150 mm; Fillet_Length=8 mm  [stored 0.0262467 ft]; Fillet_Length_Ref=24 mm  [stored 0.0787402 ft]; Flange_thickness=19 mm  [stored 0.062336 ft]; H=475 mm; H3_Ref=467 mm; ID=75 mm; L=480 mm; PG_Dia=50 mm; PG_Ref=80 mm; PG_depth=11 mm; PG_height=308 mm; PG_height_1=283 mm; PG_ref=85 mm; PR_1=20 mm  [stored 0.0656168 ft]; P_lenght=68 mm; Pilot_Dia_1=31 mm  [stored 0.101706 ft]; Pilot_Dia_2=62 mm; Pilot_Dia_3=21 mm  [stored 0.0688976 ft]; Pilot_Dia_4=10 mm  [stored 0.0328084 ft]; Pilot_Dia_5=7 mm  [stored 0.0229659 ft]; Pilot_top_1=290 mm; Pilot_top_ref=25 mm  [stored 0.082021 ft]; Profile1_Height=195 mm; Profile1_Length=39 mm  [stored 0.127953 ft]; Profile1_Length_2=26 mm; Profile_Dia=8 mm  [stored 0.0262467 ft]; Profile_Dia_2=8 mm  [stored 0.0262467 ft]; Profile_Dia_3=16 mm  [stored 0.0524934 ft]; Profile_height ref=43 mm; T_Height=87 mm; T_Height_2=74 mm; T_Height_Ref_1=12 mm  [stored 0.0393701 ft]; T_Height_Ref_2=14 mm  [stored 0.0459318 ft]; Top_Profile=222 mm; Top_Profile_Ref=227 mm; W=375 mm; W_Ref=367 mm
- 879-0150-10-14400619999_DN150_PN10/16: Body_Collar_Dia=50 mm; Body_Collar_Dia_2=43 mm; Body_Flange_Dia=155 mm; Body_Flange_Dia_2=171 mm; Body_Height_1=120 mm; Body_Height_2=60 mm; Body_Height_3=68 mm; Body_Height_4=75 mm; Body_Top_Dia=22 mm  [stored 0.0721785 ft]; Body_Top_Dia_2=18 mm  [stored 0.0590551 ft]; Body_With_Dia=60 mm; Body_With_Dia_1=120 mm; Body_With_Dia_2=130 mm; Bolt_support=369 mm; Bolt_support_2=185 mm; Bolt_support_Dia=16 mm  [stored 0.0524934 ft]; Bolt_support_lenght=95 mm; Bolt_support_lenght_2=105 mm; Bottom_profile=38 mm; D1=106 mm; D3=143 mm; DN=150 mm; Fillet_Length=8 mm  [stored 0.0262467 ft]; Fillet_Length_Ref=24 mm  [stored 0.0787402 ft]; Flange_thickness=19 mm  [stored 0.062336 ft]; H=475 mm; H3_Ref=467 mm; ID=75 mm; L=480 mm; PG_Dia=50 mm; PG_Ref=80 mm; PG_depth=11 mm; PG_height=308 mm; PG_height_1=283 mm; PG_ref=85 mm; PR_1=20 mm  [stored 0.0656168 ft]; P_lenght=68 mm; Pilot_Dia_1=31 mm  [stored 0.101706 ft]; Pilot_Dia_2=62 mm; Pilot_Dia_3=21 mm  [stored 0.0688976 ft]; Pilot_Dia_4=10 mm  [stored 0.0328084 ft]; Pilot_Dia_5=7 mm  [stored 0.0229659 ft]; Pilot_top_1=294 mm; Pilot_top_ref=21 mm  [stored 0.0688976 ft]; Profile1_Height=195 mm; Profile1_Length=39 mm  [stored 0.127953 ft]; Profile1_Length_2=26 mm; Profile_Dia=8 mm  [stored 0.0262467 ft]; Profile_Dia_2=8 mm  [stored 0.0262467 ft]; Profile_Dia_3=16 mm  [stored 0.0524934 ft]; Profile_height ref=43 mm; T_Height=87 mm; T_Height_2=74 mm; T_Height_Ref_1=12 mm  [stored 0.0393701 ft]; T_Height_Ref_2=14 mm  [stored 0.0459318 ft]; Top_Profile=222 mm; Top_Profile_Ref=227 mm; W=375 mm; W_Ref=367 mm
- 879-0150-10-14400629999_DN150_PN10/16: Body_Collar_Dia=50 mm; Body_Collar_Dia_2=43 mm; Body_Flange_Dia=155 mm; Body_Flange_Dia_2=171 mm; Body_Height_1=120 mm; Body_Height_2=60 mm; Body_Height_3=60 mm; Body_Height_4=75 mm; Body_Top_Dia=22 mm  [stored 0.0721785 ft]; Body_Top_Dia_2=18 mm  [stored 0.0590551 ft]; Body_With_Dia=60 mm; Body_With_Dia_1=120 mm; Body_With_Dia_2=130 mm; Bolt_support=369 mm; Bolt_support_2=185 mm; Bolt_support_Dia=16 mm  [stored 0.0524934 ft]; Bolt_support_lenght=95 mm; Bolt_support_lenght_2=105 mm; Bottom_profile=38 mm; D1=106 mm; D3=143 mm; DN=150 mm; Fillet_Length=8 mm  [stored 0.0262467 ft]; Fillet_Length_Ref=24 mm  [stored 0.0787402 ft]; Flange_thickness=19 mm  [stored 0.062336 ft]; H=475 mm; H3_Ref=467 mm; ID=75 mm; L=480 mm; PG_Dia=50 mm; PG_Ref=80 mm; PG_depth=11 mm; PG_height=308 mm; PG_height_1=283 mm; PG_ref=85 mm; PR_1=20 mm  [stored 0.0656168 ft]; P_lenght=68 mm; Pilot_Dia_1=31 mm  [stored 0.101706 ft]; Pilot_Dia_2=62 mm; Pilot_Dia_3=21 mm  [stored 0.0688976 ft]; Pilot_Dia_4=10 mm  [stored 0.0328084 ft]; Pilot_Dia_5=7 mm  [stored 0.0229659 ft]; Pilot_top_1=290 mm; Pilot_top_ref=25 mm  [stored 0.082021 ft]; Profile1_Height=195 mm; Profile1_Length=39 mm  [stored 0.127953 ft]; Profile1_Length_2=26 mm; Profile_Dia=8 mm  [stored 0.0262467 ft]; Profile_Dia_2=8 mm  [stored 0.0262467 ft]; Profile_Dia_3=16 mm  [stored 0.0524934 ft]; Profile_height ref=43 mm; T_Height=87 mm; T_Height_2=74 mm; T_Height_Ref_1=12 mm  [stored 0.0393701 ft]; T_Height_Ref_2=14 mm  [stored 0.0459318 ft]; Top_Profile=222 mm; Top_Profile_Ref=227 mm; W=375 mm; W_Ref=367 mm
- 879-0150-10-144006299A0_DN150_PN10/16: Body_Collar_Dia=50 mm; Body_Collar_Dia_2=43 mm; Body_Flange_Dia=155 mm; Body_Flange_Dia_2=171 mm; Body_Height_1=120 mm; Body_Height_2=60 mm; Body_Height_3=68 mm; Body_Height_4=75 mm; Body_Top_Dia=22 mm  [stored 0.0721785 ft]; Body_Top_Dia_2=18 mm  [stored 0.0590551 ft]; Body_With_Dia=60 mm; Body_With_Dia_1=120 mm; Body_With_Dia_2=130 mm; Bolt_support=369 mm; Bolt_support_2=185 mm; Bolt_support_Dia=16 mm  [stored 0.0524934 ft]; Bolt_support_lenght=95 mm; Bolt_support_lenght_2=105 mm; Bottom_profile=38 mm; D1=106 mm; D3=143 mm; DN=150 mm; Fillet_Length=8 mm  [stored 0.0262467 ft]; Fillet_Length_Ref=24 mm  [stored 0.0787402 ft]; Flange_thickness=19 mm  [stored 0.062336 ft]; H=607 mm; H3_Ref=599 mm; ID=75 mm; L=480 mm; PG_Dia=50 mm; PG_Ref=80 mm; PG_depth=11 mm; PG_height=338 mm; PG_height_1=312 mm; PG_ref=85 mm; PR_1=49 mm; P_lenght=68 mm; Pilot_Dia_1=31 mm  [stored 0.101706 ft]; Pilot_Dia_2=62 mm; Pilot_Dia_3=21 mm  [stored 0.0688976 ft]; Pilot_Dia_4=10 mm  [stored 0.0328084 ft]; Pilot_Dia_5=7 mm  [stored 0.0229659 ft]; Pilot_top_1=360 mm; Pilot_top_ref=87 mm; Profile1_Height=195 mm; Profile1_Length=39 mm  [stored 0.127953 ft]; Profile1_Length_2=26 mm; Profile_Dia=8 mm  [stored 0.0262467 ft]; Profile_Dia_2=8 mm  [stored 0.0262467 ft]; Profile_Dia_3=16 mm  [stored 0.0524934 ft]; Profile_height ref=43 mm; T_Height=219 mm; T_Height_2=187 mm; T_Height_Ref_1=31 mm  [stored 0.101706 ft]; T_Height_Ref_2=36 mm; Top_Profile=222 mm; Top_Profile_Ref=227 mm; W=375 mm; W_Ref=367 mm
- 879-0200-10-04400609999_DN200_PN10: Body_Collar_Dia=63 mm; Body_Collar_Dia_2=54 mm; Body_Flange_Dia=194 mm; Body_Flange_Dia_2=214 mm; Body_Height_1=150 mm; Body_Height_2=75 mm; Body_Height_3=75 mm; Body_Height_4=90 mm; Body_Top_Dia=27 mm; Body_Top_Dia_2=22 mm  [stored 0.0721785 ft]; Body_With_Dia=75 mm; Body_With_Dia_1=150 mm; Body_With_Dia_2=162 mm; Bolt_support=462 mm; Bolt_support_2=231 mm; Bolt_support_Dia=20 mm  [stored 0.0656168 ft]; Bolt_support_lenght=120 mm; Bolt_support_lenght_2=130 mm; Bottom_profile=50 mm; D1=133 mm; D3=170 mm; DN=200 mm; Fillet_Length=10 mm  [stored 0.0328084 ft]; Fillet_Length_Ref=30 mm  [stored 0.0984252 ft]; Flange_thickness=20 mm  [stored 0.0656168 ft]; H=590 mm; H3_Ref=580 mm; ID=100 mm; L=600 mm; PG_Dia=67 mm; PG_Ref=100 mm; PG_depth=14 mm  [stored 0.0459318 ft]; PG_height=378 mm; PG_height_1=345 mm; PG_ref=110 mm; PR_1=29 mm; P_lenght=85 mm; Pilot_Dia_1=39 mm  [stored 0.127953 ft]; Pilot_Dia_2=77 mm; Pilot_Dia_3=26 mm; Pilot_Dia_4=13 mm; Pilot_Dia_5=9 mm  [stored 0.0295276 ft]; Pilot_top_1=363 mm; Pilot_top_ref=38 mm; Profile1_Height=238 mm; Profile1_Length=46 mm; Profile1_Length_2=31 mm  [stored 0.101706 ft]; Profile_Dia=10 mm  [stored 0.0328084 ft]; Profile_Dia_2=10 mm  [stored 0.0328084 ft]; Profile_Dia_3=20 mm  [stored 0.0656168 ft]; Profile_height ref=45 mm; T_Height=127 mm; T_Height_2=109 mm; T_Height_Ref_1=18 mm  [stored 0.0590551 ft]; T_Height_Ref_2=21 mm  [stored 0.0688976 ft]; Top_Profile=277 mm; Top_Profile_Ref=282 mm; W=440 mm; W_Ref=430 mm
- 879-0200-10-04400619999_DN200_PN10: Body_Collar_Dia=63 mm; Body_Collar_Dia_2=54 mm; Body_Flange_Dia=194 mm; Body_Flange_Dia_2=214 mm; Body_Height_1=150 mm; Body_Height_2=75 mm; Body_Height_3=100 mm; Body_Height_4=90 mm; Body_Top_Dia=27 mm; Body_Top_Dia_2=22 mm  [stored 0.0721785 ft]; Body_With_Dia=75 mm; Body_With_Dia_1=150 mm; Body_With_Dia_2=162 mm; Bolt_support=462 mm; Bolt_support_2=231 mm; Bolt_support_Dia=20 mm  [stored 0.0656168 ft]; Bolt_support_lenght=120 mm; Bolt_support_lenght_2=130 mm; Bottom_profile=50 mm; D1=133 mm; D3=170 mm; DN=200 mm; Fillet_Length=10 mm  [stored 0.0328084 ft]; Fillet_Length_Ref=30 mm  [stored 0.0984252 ft]; Flange_thickness=20 mm  [stored 0.0656168 ft]; H=590 mm; H3_Ref=580 mm; ID=100 mm; L=600 mm; PG_Dia=67 mm; PG_Ref=100 mm; PG_depth=14 mm  [stored 0.0459318 ft]; PG_height=380 mm; PG_height_1=347 mm; PG_ref=110 mm; PR_1=28 mm; P_lenght=85 mm; Pilot_Dia_1=39 mm  [stored 0.127953 ft]; Pilot_Dia_2=77 mm; Pilot_Dia_3=26 mm; Pilot_Dia_4=13 mm; Pilot_Dia_5=9 mm  [stored 0.0295276 ft]; Pilot_top_1=375 mm; Pilot_top_ref=25 mm  [stored 0.082021 ft]; Profile1_Height=240 mm; Profile1_Length=46 mm; Profile1_Length_2=31 mm  [stored 0.101706 ft]; Profile_Dia=10 mm  [stored 0.0328084 ft]; Profile_Dia_2=10 mm  [stored 0.0328084 ft]; Profile_Dia_3=20 mm  [stored 0.0656168 ft]; Profile_height ref=45 mm; T_Height=125 mm; T_Height_2=107 mm; T_Height_Ref_1=18 mm  [stored 0.0590551 ft]; T_Height_Ref_2=21 mm  [stored 0.0688976 ft]; Top_Profile=277 mm; Top_Profile_Ref=282 mm; W=440 mm; W_Ref=430 mm
- 879-0200-10-04400629999_DN200_PN10: Body_Collar_Dia=63 mm; Body_Collar_Dia_2=54 mm; Body_Flange_Dia=194 mm; Body_Flange_Dia_2=214 mm; Body_Height_1=150 mm; Body_Height_2=75 mm; Body_Height_3=75 mm; Body_Height_4=90 mm; Body_Top_Dia=27 mm; Body_Top_Dia_2=22 mm  [stored 0.0721785 ft]; Body_With_Dia=75 mm; Body_With_Dia_1=150 mm; Body_With_Dia_2=162 mm; Bolt_support=462 mm; Bolt_support_2=231 mm; Bolt_support_Dia=20 mm  [stored 0.0656168 ft]; Bolt_support_lenght=120 mm; Bolt_support_lenght_2=130 mm; Bottom_profile=50 mm; D1=133 mm; D3=170 mm; DN=200 mm; Fillet_Length=10 mm  [stored 0.0328084 ft]; Fillet_Length_Ref=30 mm  [stored 0.0984252 ft]; Flange_thickness=20 mm  [stored 0.0656168 ft]; H=590 mm; H3_Ref=580 mm; ID=100 mm; L=600 mm; PG_Dia=67 mm; PG_Ref=100 mm; PG_depth=14 mm  [stored 0.0459318 ft]; PG_height=378 mm; PG_height_1=345 mm; PG_ref=110 mm; PR_1=29 mm; P_lenght=85 mm; Pilot_Dia_1=39 mm  [stored 0.127953 ft]; Pilot_Dia_2=77 mm; Pilot_Dia_3=26 mm; Pilot_Dia_4=13 mm; Pilot_Dia_5=9 mm  [stored 0.0295276 ft]; Pilot_top_1=363 mm; Pilot_top_ref=38 mm; Profile1_Height=238 mm; Profile1_Length=46 mm; Profile1_Length_2=31 mm  [stored 0.101706 ft]; Profile_Dia=10 mm  [stored 0.0328084 ft]; Profile_Dia_2=10 mm  [stored 0.0328084 ft]; Profile_Dia_3=20 mm  [stored 0.0656168 ft]; Profile_height ref=45 mm; T_Height=127 mm; T_Height_2=109 mm; T_Height_Ref_1=18 mm  [stored 0.0590551 ft]; T_Height_Ref_2=21 mm  [stored 0.0688976 ft]; Top_Profile=277 mm; Top_Profile_Ref=282 mm; W=440 mm; W_Ref=430 mm
- 879-0200-10-044006299A0_DN200_PN10: Body_Collar_Dia=63 mm; Body_Collar_Dia_2=54 mm; Body_Flange_Dia=194 mm; Body_Flange_Dia_2=214 mm; Body_Height_1=150 mm; Body_Height_2=75 mm; Body_Height_3=86 mm; Body_Height_4=90 mm; Body_Top_Dia=27 mm; Body_Top_Dia_2=22 mm  [stored 0.0721785 ft]; Body_With_Dia=75 mm; Body_With_Dia_1=150 mm; Body_With_Dia_2=162 mm; Bolt_support=462 mm; Bolt_support_2=231 mm; Bolt_support_Dia=20 mm  [stored 0.0656168 ft]; Bolt_support_lenght=120 mm; Bolt_support_lenght_2=130 mm; Bottom_profile=50 mm; D1=133 mm; D3=170 mm; DN=200 mm; Fillet_Length=10 mm  [stored 0.0328084 ft]; Fillet_Length_Ref=30 mm  [stored 0.0984252 ft]; Flange_thickness=20 mm  [stored 0.0656168 ft]; H=774 mm; H3_Ref=764 mm; ID=100 mm; L=600 mm; PG_Dia=67 mm; PG_Ref=100 mm; PG_depth=14 mm  [stored 0.0459318 ft]; PG_height=422 mm; PG_height_1=388 mm; PG_ref=110 mm; PR_1=70 mm; P_lenght=85 mm; Pilot_Dia_1=39 mm  [stored 0.127953 ft]; Pilot_Dia_2=77 mm; Pilot_Dia_3=26 mm; Pilot_Dia_4=13 mm; Pilot_Dia_5=9 mm  [stored 0.0295276 ft]; Pilot_top_1=460 mm; Pilot_top_ref=124 mm; Profile1_Height=240 mm; Profile1_Length=46 mm; Profile1_Length_2=31 mm  [stored 0.101706 ft]; Profile_Dia=10 mm  [stored 0.0328084 ft]; Profile_Dia_2=10 mm  [stored 0.0328084 ft]; Profile_Dia_3=20 mm  [stored 0.0656168 ft]; Profile_height ref=45 mm; T_Height=309 mm; T_Height_2=265 mm; T_Height_Ref_1=44 mm; T_Height_Ref_2=52 mm; Top_Profile=277 mm; Top_Profile_Ref=282 mm; W=440 mm; W_Ref=430 mm
- 879-0200-10-14400609999_DN200_PN16: Body_Collar_Dia=63 mm; Body_Collar_Dia_2=54 mm; Body_Flange_Dia=194 mm; Body_Flange_Dia_2=214 mm; Body_Height_1=150 mm; Body_Height_2=75 mm; Body_Height_3=75 mm; Body_Height_4=90 mm; Body_Top_Dia=27 mm; Body_Top_Dia_2=22 mm  [stored 0.0721785 ft]; Body_With_Dia=75 mm; Body_With_Dia_1=150 mm; Body_With_Dia_2=162 mm; Bolt_support=462 mm; Bolt_support_2=231 mm; Bolt_support_Dia=20 mm  [stored 0.0656168 ft]; Bolt_support_lenght=120 mm; Bolt_support_lenght_2=130 mm; Bottom_profile=50 mm; D1=133 mm; D3=170 mm; DN=200 mm; Fillet_Length=10 mm  [stored 0.0328084 ft]; Fillet_Length_Ref=30 mm  [stored 0.0984252 ft]; Flange_thickness=20 mm  [stored 0.0656168 ft]; H=590 mm; H3_Ref=580 mm; ID=100 mm; L=600 mm; PG_Dia=67 mm; PG_Ref=100 mm; PG_depth=14 mm  [stored 0.0459318 ft]; PG_height=379 mm; PG_height_1=345 mm; PG_ref=110 mm; PR_1=29 mm; P_lenght=85 mm; Pilot_Dia_1=39 mm  [stored 0.127953 ft]; Pilot_Dia_2=77 mm; Pilot_Dia_3=26 mm; Pilot_Dia_4=13 mm; Pilot_Dia_5=9 mm  [stored 0.0295276 ft]; Pilot_top_1=363 mm; Pilot_top_ref=38 mm; Profile1_Height=238 mm; Profile1_Length=46 mm; Profile1_Length_2=31 mm  [stored 0.101706 ft]; Profile_Dia=10 mm  [stored 0.0328084 ft]; Profile_Dia_2=10 mm  [stored 0.0328084 ft]; Profile_Dia_3=20 mm  [stored 0.0656168 ft]; Profile_height ref=45 mm; T_Height=127 mm; T_Height_2=109 mm; T_Height_Ref_1=18 mm  [stored 0.0590551 ft]; T_Height_Ref_2=21 mm  [stored 0.0688976 ft]; Top_Profile=277 mm; Top_Profile_Ref=282 mm; W=440 mm; W_Ref=430 mm
- 879-0200-10-14400619999_DN200_PN16: Body_Collar_Dia=63 mm; Body_Collar_Dia_2=54 mm; Body_Flange_Dia=194 mm; Body_Flange_Dia_2=214 mm; Body_Height_1=150 mm; Body_Height_2=75 mm; Body_Height_3=100 mm; Body_Height_4=90 mm; Body_Top_Dia=27 mm; Body_Top_Dia_2=22 mm  [stored 0.0721785 ft]; Body_With_Dia=75 mm; Body_With_Dia_1=150 mm; Body_With_Dia_2=162 mm; Bolt_support=462 mm; Bolt_support_2=231 mm; Bolt_support_Dia=20 mm  [stored 0.0656168 ft]; Bolt_support_lenght=120 mm; Bolt_support_lenght_2=130 mm; Bottom_profile=50 mm; D1=133 mm; D3=170 mm; DN=201 mm; Fillet_Length=10 mm  [stored 0.0328084 ft]; Fillet_Length_Ref=30 mm  [stored 0.0984252 ft]; Flange_thickness=20 mm  [stored 0.0656168 ft]; H=590 mm; H3_Ref=580 mm; ID=100 mm; L=600 mm; PG_Dia=67 mm; PG_Ref=100 mm; PG_depth=14 mm  [stored 0.0459318 ft]; PG_height=380 mm; PG_height_1=347 mm; PG_ref=110 mm; PR_1=28 mm; P_lenght=85 mm; Pilot_Dia_1=39 mm  [stored 0.127953 ft]; Pilot_Dia_2=77 mm; Pilot_Dia_3=26 mm; Pilot_Dia_4=13 mm; Pilot_Dia_5=9 mm  [stored 0.0295276 ft]; Pilot_top_1=375 mm; Pilot_top_ref=25 mm  [stored 0.082021 ft]; Profile1_Height=240 mm; Profile1_Length=46 mm; Profile1_Length_2=31 mm  [stored 0.101706 ft]; Profile_Dia=10 mm  [stored 0.0328084 ft]; Profile_Dia_2=10 mm  [stored 0.0328084 ft]; Profile_Dia_3=20 mm  [stored 0.0656168 ft]; Profile_height ref=45 mm; T_Height=125 mm; T_Height_2=107 mm; T_Height_Ref_1=18 mm  [stored 0.0590551 ft]; T_Height_Ref_2=21 mm  [stored 0.0688976 ft]; Top_Profile=277 mm; Top_Profile_Ref=282 mm; W=440 mm; W_Ref=430 mm
- 879-0200-10-14400629999_DN200_PN16: Body_Collar_Dia=63 mm; Body_Collar_Dia_2=54 mm; Body_Flange_Dia=194 mm; Body_Flange_Dia_2=214 mm; Body_Height_1=150 mm; Body_Height_2=75 mm; Body_Height_3=75 mm; Body_Height_4=90 mm; Body_Top_Dia=27 mm; Body_Top_Dia_2=22 mm  [stored 0.0721785 ft]; Body_With_Dia=75 mm; Body_With_Dia_1=150 mm; Body_With_Dia_2=162 mm; Bolt_support=462 mm; Bolt_support_2=231 mm; Bolt_support_Dia=20 mm  [stored 0.0656168 ft]; Bolt_support_lenght=120 mm; Bolt_support_lenght_2=130 mm; Bottom_profile=50 mm; D1=133 mm; D3=170 mm; DN=201 mm; Fillet_Length=10 mm  [stored 0.0328084 ft]; Fillet_Length_Ref=30 mm  [stored 0.0984252 ft]; Flange_thickness=20 mm  [stored 0.0656168 ft]; H=590 mm; H3_Ref=580 mm; ID=100 mm; L=600 mm; PG_Dia=67 mm; PG_Ref=100 mm; PG_depth=14 mm  [stored 0.0459318 ft]; PG_height=379 mm; PG_height_1=345 mm; PG_ref=110 mm; PR_1=29 mm; P_lenght=85 mm; Pilot_Dia_1=39 mm  [stored 0.127953 ft]; Pilot_Dia_2=77 mm; Pilot_Dia_3=26 mm; Pilot_Dia_4=13 mm; Pilot_Dia_5=9 mm  [stored 0.0295276 ft]; Pilot_top_1=363 mm; Pilot_top_ref=38 mm; Profile1_Height=238 mm; Profile1_Length=46 mm; Profile1_Length_2=31 mm  [stored 0.101706 ft]; Profile_Dia=10 mm  [stored 0.0328084 ft]; Profile_Dia_2=10 mm  [stored 0.0328084 ft]; Profile_Dia_3=20 mm  [stored 0.0656168 ft]; Profile_height ref=45 mm; T_Height=127 mm; T_Height_2=109 mm; T_Height_Ref_1=18 mm  [stored 0.0590551 ft]; T_Height_Ref_2=21 mm  [stored 0.0688976 ft]; Top_Profile=277 mm; Top_Profile_Ref=282 mm; W=440 mm; W_Ref=430 mm
- 879-0200-10-144006299A0_DN200_PN16: Body_Collar_Dia=63 mm; Body_Collar_Dia_2=54 mm; Body_Flange_Dia=194 mm; Body_Flange_Dia_2=214 mm; Body_Height_1=150 mm; Body_Height_2=75 mm; Body_Height_3=86 mm; Body_Height_4=90 mm; Body_Top_Dia=27 mm; Body_Top_Dia_2=22 mm  [stored 0.0721785 ft]; Body_With_Dia=75 mm; Body_With_Dia_1=150 mm; Body_With_Dia_2=162 mm; Bolt_support=462 mm; Bolt_support_2=231 mm; Bolt_support_Dia=20 mm  [stored 0.0656168 ft]; Bolt_support_lenght=120 mm; Bolt_support_lenght_2=130 mm; Bottom_profile=50 mm; D1=133 mm; D3=170 mm; DN=201 mm; Fillet_Length=10 mm  [stored 0.0328084 ft]; Fillet_Length_Ref=30 mm  [stored 0.0984252 ft]; Flange_thickness=20 mm  [stored 0.0656168 ft]; H=774 mm; H3_Ref=764 mm; ID=100 mm; L=600 mm; PG_Dia=67 mm; PG_Ref=100 mm; PG_depth=14 mm  [stored 0.0459318 ft]; PG_height=422 mm; PG_height_1=388 mm; PG_ref=110 mm; PR_1=70 mm; P_lenght=85 mm; Pilot_Dia_1=39 mm  [stored 0.127953 ft]; Pilot_Dia_2=77 mm; Pilot_Dia_3=26 mm; Pilot_Dia_4=13 mm; Pilot_Dia_5=9 mm  [stored 0.0295276 ft]; Pilot_top_1=460 mm; Pilot_top_ref=124 mm; Profile1_Height=240 mm; Profile1_Length=46 mm; Profile1_Length_2=31 mm  [stored 0.101706 ft]; Profile_Dia=10 mm  [stored 0.0328084 ft]; Profile_Dia_2=10 mm  [stored 0.0328084 ft]; Profile_Dia_3=20 mm  [stored 0.0656168 ft]; Profile_height ref=45 mm; T_Height=309 mm; T_Height_2=265 mm; T_Height_Ref_1=44 mm; T_Height_Ref_2=52 mm; Top_Profile=277 mm; Top_Profile_Ref=282 mm; W=440 mm; W_Ref=430 mm
- 879-0250-10-04400609999_DN250_PN10: Body_Collar_Dia=76 mm; Body_Collar_Dia_2=65 mm; Body_Flange_Dia=235 mm; Body_Flange_Dia_2=261 mm; Body_Height_1=183 mm; Body_Height_2=91 mm; Body_Height_3=81 mm; Body_Height_4=106 mm; Body_Top_Dia=33 mm  [stored 0.108268 ft]; Body_Top_Dia_2=27 mm; Body_With_Dia=91 mm; Body_With_Dia_1=183 mm; Body_With_Dia_2=197 mm; Bolt_support=562 mm; Bolt_support_2=281 mm; Bolt_support_Dia=20 mm  [stored 0.0656168 ft]; Bolt_support_lenght=145 mm; Bolt_support_lenght_2=155 mm; Bottom_profile=63 mm; D1=160 mm; D3=198 mm; DN=250 mm; Fillet_Length=10 mm  [stored 0.0328084 ft]; Fillet_Length_Ref=30 mm  [stored 0.0984252 ft]; Flange_thickness=22 mm  [stored 0.0721785 ft]; H=670 mm; H3_Ref=660 mm; ID=125 mm; L=730 mm; PG_Dia=83 mm; PG_Ref=122 mm; PG_depth=14 mm  [stored 0.0459318 ft]; PG_height=449 mm; PG_height_1=407 mm; PG_ref=135 mm; PR_1=28 mm; P_lenght=101 mm; Pilot_Dia_1=46 mm; Pilot_Dia_2=92 mm; Pilot_Dia_3=31 mm  [stored 0.101706 ft]; Pilot_Dia_4=15 mm  [stored 0.0492126 ft]; Pilot_Dia_5=10 mm  [stored 0.0328084 ft]; Pilot_top_1=416 mm; Pilot_top_ref=36 mm; Profile1_Height=292 mm; Profile1_Length=53 mm; Profile1_Length_2=36 mm; Profile_Dia=10 mm  [stored 0.0328084 ft]; Profile_Dia_2=10 mm  [stored 0.0328084 ft]; Profile_Dia_3=20 mm  [stored 0.0656168 ft]; Profile_height ref=45 mm; T_Height=126 mm; T_Height_2=108 mm; T_Height_Ref_1=18 mm  [stored 0.0590551 ft]; T_Height_Ref_2=21 mm  [stored 0.0688976 ft]; Top_Profile=337 mm; Top_Profile_Ref=342 mm; W=515 mm; W_Ref=505 mm
- 879-0250-10-04400619999_DN250_PN10: Body_Collar_Dia=76 mm; Body_Collar_Dia_2=65 mm; Body_Flange_Dia=235 mm; Body_Flange_Dia_2=261 mm; Body_Height_1=183 mm; Body_Height_2=91 mm; Body_Height_3=105 mm; Body_Height_4=106 mm; Body_Top_Dia=33 mm  [stored 0.108268 ft]; Body_Top_Dia_2=27 mm; Body_With_Dia=91 mm; Body_With_Dia_1=183 mm; Body_With_Dia_2=197 mm; Bolt_support=562 mm; Bolt_support_2=281 mm; Bolt_support_Dia=20 mm  [stored 0.0656168 ft]; Bolt_support_lenght=145 mm; Bolt_support_lenght_2=155 mm; Bottom_profile=63 mm; D1=160 mm; D3=198 mm; DN=250 mm; Fillet_Length=10 mm  [stored 0.0328084 ft]; Fillet_Length_Ref=30 mm  [stored 0.0984252 ft]; Flange_thickness=22 mm  [stored 0.0721785 ft]; H=670 mm; H3_Ref=660 mm; ID=125 mm; L=730 mm; PG_Dia=83 mm; PG_Ref=122 mm; PG_depth=14 mm  [stored 0.0459318 ft]; PG_height=451 mm; PG_height_1=409 mm; PG_ref=135 mm; PR_1=28 mm; P_lenght=101 mm; Pilot_Dia_1=46 mm; Pilot_Dia_2=92 mm; Pilot_Dia_3=31 mm  [stored 0.101706 ft]; Pilot_Dia_4=15 mm  [stored 0.0492126 ft]; Pilot_Dia_5=10 mm  [stored 0.0328084 ft]; Pilot_top_1=428 mm; Pilot_top_ref=25 mm  [stored 0.082021 ft]; Profile1_Height=295 mm; Profile1_Length=53 mm; Profile1_Length_2=36 mm; Profile_Dia=10 mm  [stored 0.0328084 ft]; Profile_Dia_2=10 mm  [stored 0.0328084 ft]; Profile_Dia_3=20 mm  [stored 0.0656168 ft]; Profile_height ref=45 mm; T_Height=123 mm; T_Height_2=105 mm; T_Height_Ref_1=18 mm  [stored 0.0590551 ft]; T_Height_Ref_2=20 mm  [stored 0.0656168 ft]; Top_Profile=337 mm; Top_Profile_Ref=342 mm; W=515 mm; W_Ref=505 mm
- 879-0250-10-04400629999_DN250_PN10: Body_Collar_Dia=76 mm; Body_Collar_Dia_2=65 mm; Body_Flange_Dia=235 mm; Body_Flange_Dia_2=261 mm; Body_Height_1=183 mm; Body_Height_2=91 mm; Body_Height_3=81 mm; Body_Height_4=106 mm; Body_Top_Dia=33 mm  [stored 0.108268 ft]; Body_Top_Dia_2=27 mm; Body_With_Dia=91 mm; Body_With_Dia_1=183 mm; Body_With_Dia_2=197 mm; Bolt_support=562 mm; Bolt_support_2=281 mm; Bolt_support_Dia=20 mm  [stored 0.0656168 ft]; Bolt_support_lenght=145 mm; Bolt_support_lenght_2=155 mm; Bottom_profile=63 mm; D1=160 mm; D3=198 mm; DN=250 mm; Fillet_Length=10 mm  [stored 0.0328084 ft]; Fillet_Length_Ref=30 mm  [stored 0.0984252 ft]; Flange_thickness=22 mm  [stored 0.0721785 ft]; H=670 mm; H3_Ref=660 mm; ID=125 mm; L=730 mm; PG_Dia=83 mm; PG_Ref=122 mm; PG_depth=14 mm  [stored 0.0459318 ft]; PG_height=455 mm; PG_height_1=413 mm; PG_ref=135 mm; PR_1=27 mm; P_lenght=103 mm; Pilot_Dia_1=47 mm; Pilot_Dia_2=94 mm; Pilot_Dia_3=31 mm  [stored 0.101706 ft]; Pilot_Dia_4=16 mm  [stored 0.0524934 ft]; Pilot_Dia_5=10 mm  [stored 0.0328084 ft]; Pilot_top_1=416 mm; Pilot_top_ref=36 mm; Profile1_Height=300 mm; Profile1_Length=53 mm; Profile1_Length_2=36 mm; Profile_Dia=10 mm  [stored 0.0328084 ft]; Profile_Dia_2=10 mm  [stored 0.0328084 ft]; Profile_Dia_3=20 mm  [stored 0.0656168 ft]; Profile_height ref=45 mm; T_Height=118 mm; T_Height_2=101 mm; T_Height_Ref_1=17 mm; T_Height_Ref_2=20 mm  [stored 0.0656168 ft]; Top_Profile=337 mm; Top_Profile_Ref=342 mm; W=515 mm; W_Ref=505 mm
- 879-0250-10-044006299A0_DN250_PN10: Body_Collar_Dia=76 mm; Body_Collar_Dia_2=65 mm; Body_Flange_Dia=235 mm; Body_Flange_Dia_2=261 mm; Body_Height_1=183 mm; Body_Height_2=91 mm; Body_Height_3=81 mm; Body_Height_4=106 mm; Body_Top_Dia=33 mm  [stored 0.108268 ft]; Body_Top_Dia_2=27 mm; Body_With_Dia=91 mm; Body_With_Dia_1=183 mm; Body_With_Dia_2=197 mm; Bolt_support=562 mm; Bolt_support_2=281 mm; Bolt_support_Dia=20 mm  [stored 0.0656168 ft]; Bolt_support_lenght=145 mm; Bolt_support_lenght_2=155 mm; Bottom_profile=63 mm; D1=160 mm; D3=198 mm; DN=250 mm; Fillet_Length=10 mm  [stored 0.0328084 ft]; Fillet_Length_Ref=30 mm  [stored 0.0984252 ft]; Flange_thickness=22 mm  [stored 0.0721785 ft]; H=854 mm; H3_Ref=844 mm; ID=125 mm; L=730 mm; PG_Dia=83 mm; PG_Ref=122 mm; PG_depth=14 mm  [stored 0.0459318 ft]; PG_height=508 mm; PG_height_1=467 mm; PG_ref=135 mm; PR_1=65 mm; P_lenght=103 mm; Pilot_Dia_1=47 mm; Pilot_Dia_2=94 mm; Pilot_Dia_3=31 mm  [stored 0.101706 ft]; Pilot_Dia_4=16 mm  [stored 0.0524934 ft]; Pilot_Dia_5=10 mm  [stored 0.0328084 ft]; Pilot_top_1=508 mm; Pilot_top_ref=128 mm; Profile1_Height=315 mm; Profile1_Length=53 mm; Profile1_Length_2=36 mm; Profile_Dia=10 mm  [stored 0.0328084 ft]; Profile_Dia_2=10 mm  [stored 0.0328084 ft]; Profile_Dia_3=20 mm  [stored 0.0656168 ft]; Profile_height ref=45 mm; T_Height=287 mm; T_Height_2=246 mm; T_Height_Ref_1=41 mm; T_Height_Ref_2=48 mm; Top_Profile=337 mm; Top_Profile_Ref=342 mm; W=515 mm; W_Ref=505 mm
- 879-0250-10-14400609999_DN250_PN16: Body_Collar_Dia=76 mm; Body_Collar_Dia_2=65 mm; Body_Flange_Dia=235 mm; Body_Flange_Dia_2=261 mm; Body_Height_1=183 mm; Body_Height_2=91 mm; Body_Height_3=81 mm; Body_Height_4=106 mm; Body_Top_Dia=33 mm  [stored 0.108268 ft]; Body_Top_Dia_2=27 mm; Body_With_Dia=91 mm; Body_With_Dia_1=183 mm; Body_With_Dia_2=197 mm; Bolt_support=562 mm; Bolt_support_2=281 mm; Bolt_support_Dia=20 mm  [stored 0.0656168 ft]; Bolt_support_lenght=145 mm; Bolt_support_lenght_2=155 mm; Bottom_profile=63 mm; D1=160 mm; D3=203 mm; DN=250 mm; Fillet_Length=10 mm  [stored 0.0328084 ft]; Fillet_Length_Ref=30 mm  [stored 0.0984252 ft]; Flange_thickness=22 mm  [stored 0.0721785 ft]; H=670 mm; H3_Ref=660 mm; ID=125 mm; L=730 mm; PG_Dia=83 mm; PG_Ref=122 mm; PG_depth=14 mm  [stored 0.0459318 ft]; PG_height=448 mm; PG_height_1=406 mm; PG_ref=135 mm; PR_1=27 mm; P_lenght=101 mm; Pilot_Dia_1=46 mm; Pilot_Dia_2=92 mm; Pilot_Dia_3=31 mm  [stored 0.101706 ft]; Pilot_Dia_4=15 mm  [stored 0.0492126 ft]; Pilot_Dia_5=10 mm  [stored 0.0328084 ft]; Pilot_top_1=414 mm; Pilot_top_ref=34 mm; Profile1_Height=292 mm; Profile1_Length=55 mm; Profile1_Length_2=36 mm; Profile_Dia=10 mm  [stored 0.0328084 ft]; Profile_Dia_2=10 mm  [stored 0.0328084 ft]; Profile_Dia_3=20 mm  [stored 0.0656168 ft]; Profile_height ref=45 mm; T_Height=121 mm; T_Height_2=103 mm; T_Height_Ref_1=17 mm; T_Height_Ref_2=20 mm  [stored 0.0656168 ft]; Top_Profile=337 mm; Top_Profile_Ref=342 mm; W=515 mm; W_Ref=505 mm
- 879-0250-10-14400619999_DN250_PN16: Body_Collar_Dia=76 mm; Body_Collar_Dia_2=65 mm; Body_Flange_Dia=235 mm; Body_Flange_Dia_2=261 mm; Body_Height_1=183 mm; Body_Height_2=91 mm; Body_Height_3=105 mm; Body_Height_4=106 mm; Body_Top_Dia=33 mm  [stored 0.108268 ft]; Body_Top_Dia_2=27 mm; Body_With_Dia=91 mm; Body_With_Dia_1=183 mm; Body_With_Dia_2=197 mm; Bolt_support=562 mm; Bolt_support_2=281 mm; Bolt_support_Dia=20 mm  [stored 0.0656168 ft]; Bolt_support_lenght=145 mm; Bolt_support_lenght_2=155 mm; Bottom_profile=63 mm; D1=160 mm; D3=203 mm; DN=251 mm; Fillet_Length=10 mm  [stored 0.0328084 ft]; Fillet_Length_Ref=30 mm  [stored 0.0984252 ft]; Flange_thickness=22 mm  [stored 0.0721785 ft]; H=670 mm; H3_Ref=660 mm; ID=125 mm; L=730 mm; PG_Dia=84 mm; PG_Ref=122 mm; PG_depth=14 mm  [stored 0.0459318 ft]; PG_height=450 mm; PG_height_1=408 mm; PG_ref=135 mm; PR_1=27 mm; P_lenght=101 mm; Pilot_Dia_1=46 mm; Pilot_Dia_2=92 mm; Pilot_Dia_3=31 mm  [stored 0.101706 ft]; Pilot_Dia_4=15 mm  [stored 0.0492126 ft]; Pilot_Dia_5=10 mm  [stored 0.0328084 ft]; Pilot_top_1=425 mm; Pilot_top_ref=22 mm  [stored 0.0721785 ft]; Profile1_Height=295 mm; Profile1_Length=55 mm; Profile1_Length_2=36 mm; Profile_Dia=10 mm  [stored 0.0328084 ft]; Profile_Dia_2=10 mm  [stored 0.0328084 ft]; Profile_Dia_3=20 mm  [stored 0.0656168 ft]; Profile_height ref=45 mm; T_Height=118 mm; T_Height_2=101 mm; T_Height_Ref_1=17 mm; T_Height_Ref_2=20 mm  [stored 0.0656168 ft]; Top_Profile=337 mm; Top_Profile_Ref=342 mm; W=515 mm; W_Ref=505 mm
- 879-0250-10-14400629999_DN250_PN16: Body_Collar_Dia=76 mm; Body_Collar_Dia_2=65 mm; Body_Flange_Dia=235 mm; Body_Flange_Dia_2=261 mm; Body_Height_1=183 mm; Body_Height_2=91 mm; Body_Height_3=81 mm; Body_Height_4=106 mm; Body_Top_Dia=33 mm  [stored 0.108268 ft]; Body_Top_Dia_2=27 mm; Body_With_Dia=91 mm; Body_With_Dia_1=183 mm; Body_With_Dia_2=197 mm; Bolt_support=562 mm; Bolt_support_2=281 mm; Bolt_support_Dia=20 mm  [stored 0.0656168 ft]; Bolt_support_lenght=145 mm; Bolt_support_lenght_2=155 mm; Bottom_profile=63 mm; D1=160 mm; D3=203 mm; DN=251 mm; Fillet_Length=10 mm  [stored 0.0328084 ft]; Fillet_Length_Ref=30 mm  [stored 0.0984252 ft]; Flange_thickness=22 mm  [stored 0.0721785 ft]; H=670 mm; H3_Ref=660 mm; ID=125 mm; L=730 mm; PG_Dia=84 mm; PG_Ref=122 mm; PG_depth=14 mm  [stored 0.0459318 ft]; PG_height=454 mm; PG_height_1=412 mm; PG_ref=135 mm; PR_1=25 mm  [stored 0.082021 ft]; P_lenght=103 mm; Pilot_Dia_1=47 mm; Pilot_Dia_2=94 mm; Pilot_Dia_3=31 mm  [stored 0.101706 ft]; Pilot_Dia_4=16 mm  [stored 0.0524934 ft]; Pilot_Dia_5=10 mm  [stored 0.0328084 ft]; Pilot_top_1=414 mm; Pilot_top_ref=34 mm; Profile1_Height=300 mm; Profile1_Length=55 mm; Profile1_Length_2=36 mm; Profile_Dia=10 mm  [stored 0.0328084 ft]; Profile_Dia_2=10 mm  [stored 0.0328084 ft]; Profile_Dia_3=20 mm  [stored 0.0656168 ft]; Profile_height ref=45 mm; T_Height=113 mm; T_Height_2=96 mm; T_Height_Ref_1=16 mm  [stored 0.0524934 ft]; T_Height_Ref_2=19 mm  [stored 0.062336 ft]; Top_Profile=337 mm; Top_Profile_Ref=342 mm; W=515 mm; W_Ref=505 mm
- 879-0250-10-144006299A0_DN250_PN16: Body_Collar_Dia=76 mm; Body_Collar_Dia_2=65 mm; Body_Flange_Dia=235 mm; Body_Flange_Dia_2=261 mm; Body_Height_1=183 mm; Body_Height_2=91 mm; Body_Height_3=81 mm; Body_Height_4=106 mm; Body_Top_Dia=33 mm  [stored 0.108268 ft]; Body_Top_Dia_2=27 mm; Body_With_Dia=91 mm; Body_With_Dia_1=183 mm; Body_With_Dia_2=197 mm; Bolt_support=562 mm; Bolt_support_2=281 mm; Bolt_support_Dia=20 mm  [stored 0.0656168 ft]; Bolt_support_lenght=145 mm; Bolt_support_lenght_2=155 mm; Bottom_profile=63 mm; D1=160 mm; D3=203 mm; DN=251 mm; Fillet_Length=10 mm  [stored 0.0328084 ft]; Fillet_Length_Ref=30 mm  [stored 0.0984252 ft]; Flange_thickness=22 mm  [stored 0.0721785 ft]; H=854 mm; H3_Ref=844 mm; ID=125 mm; L=730 mm; PG_Dia=84 mm; PG_Ref=122 mm; PG_depth=14 mm  [stored 0.0459318 ft]; PG_height=507 mm; PG_height_1=465 mm; PG_ref=135 mm; PR_1=64 mm; P_lenght=103 mm; Pilot_Dia_1=47 mm; Pilot_Dia_2=94 mm; Pilot_Dia_3=31 mm  [stored 0.101706 ft]; Pilot_Dia_4=16 mm  [stored 0.0524934 ft]; Pilot_Dia_5=10 mm  [stored 0.0328084 ft]; Pilot_top_1=506 mm; Pilot_top_ref=126 mm; Profile1_Height=315 mm; Profile1_Length=55 mm; Profile1_Length_2=36 mm; Profile_Dia=10 mm  [stored 0.0328084 ft]; Profile_Dia_2=10 mm  [stored 0.0328084 ft]; Profile_Dia_3=20 mm  [stored 0.0656168 ft]; Profile_height ref=45 mm; T_Height=282 mm; T_Height_2=241 mm; T_Height_Ref_1=40 mm  [stored 0.131234 ft]; T_Height_Ref_2=47 mm; Top_Profile=337 mm; Top_Profile_Ref=342 mm; W=515 mm; W_Ref=505 mm

note: [stored X ft] marks values corroborated as IEEE doubles in the binary element streams (Revit-internal decimal feet)

## geometry (parser evidence)
native form markers: Sweep x3
no freeform markers — native parametric forms only
